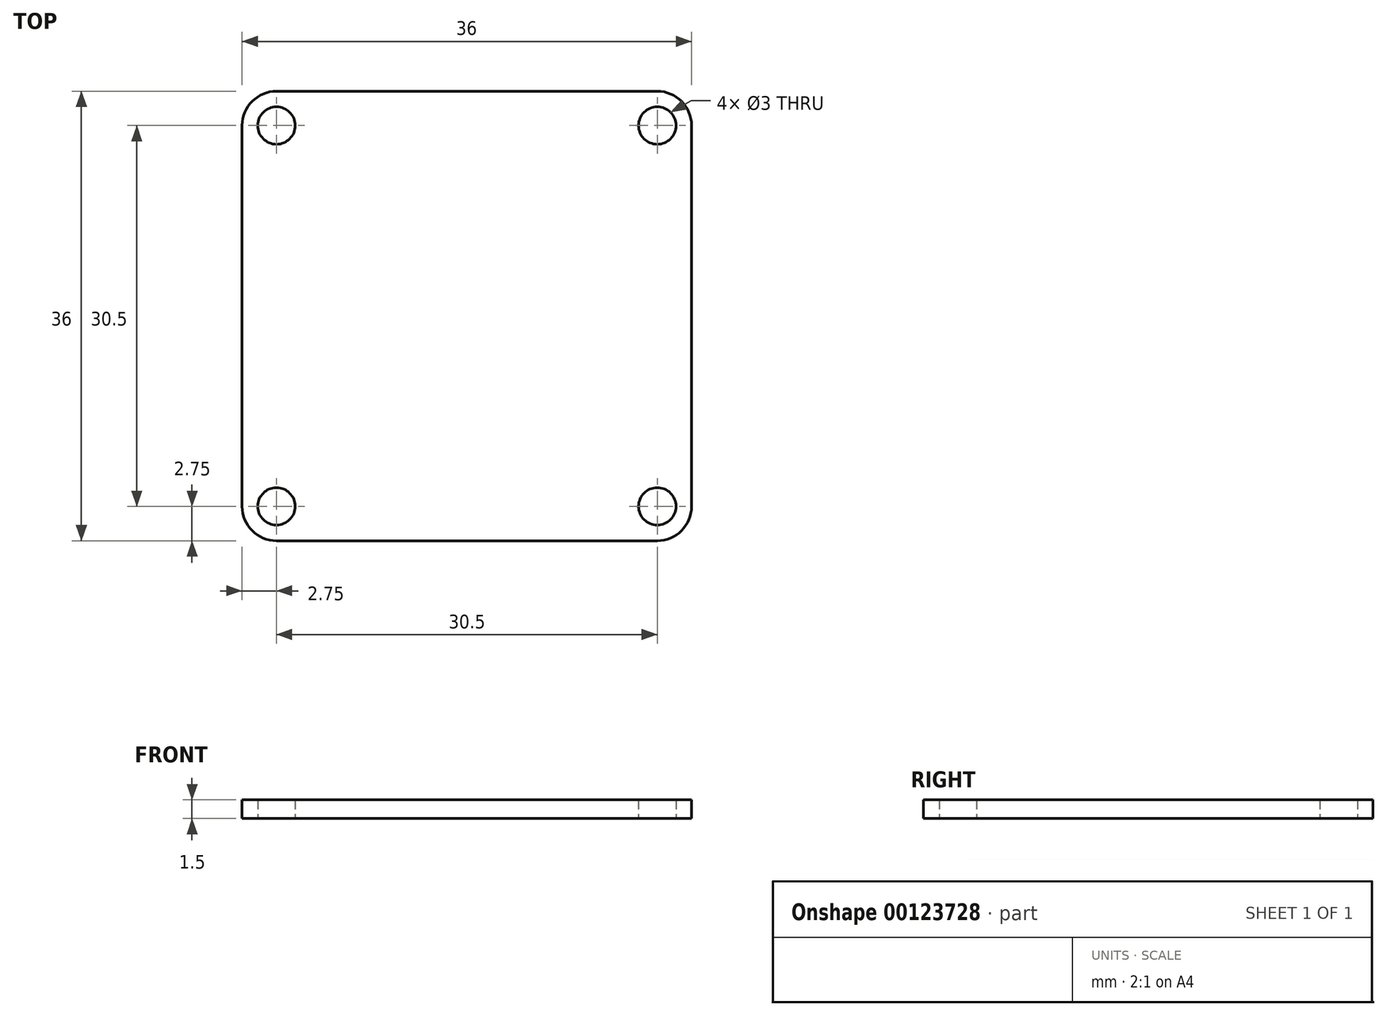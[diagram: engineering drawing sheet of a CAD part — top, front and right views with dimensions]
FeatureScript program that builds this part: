
annotation { "Feature Type Name" : "Feature", "Feature Type Description" : "" }
export const myFeature = defineFeature(function(context is Context, id is Id, definition is map)
    precondition{}
    {
        {
            var Q0;
            Q0=qCreatedBy(makeId("Top.planeOp"),FACE);
            var sketch = newSketch(context, id + "F0", { "sketchPlane" : qUnion([Q0])});
            skLineSegment(sketch, "E0.bottom", {"start": v(-15.25, 18) * mm, "end": v(15.25, 18) * mm});
            skLineSegment(sketch, "E0.top", {"start": v(-15.25, -18) * mm, "end": v(15.25, -18) * mm});
            skLineSegment(sketch, "E0.left", {"start": v(-18, 15.25) * mm, "end": v(-18, -15.25) * mm});
            skLineSegment(sketch, "E0.right", {"start": v(18, 15.25) * mm, "end": v(18, -15.25) * mm});
            skCircle(sketch, "E1", {"center": v(-15.25, 15.25) * mm, "radius": 1.5 * mm});
            skCircle(sketch, "E2.0.1.0", {"center": v(-15.25, -15.25) * mm, "radius": 1.5 * mm});
            skCircle(sketch, "E2.1.0.0", {"center": v(15.25, 15.25) * mm, "radius": 1.5 * mm});
            skCircle(sketch, "E2.1.1.0", {"center": v(15.25, -15.25) * mm, "radius": 1.5 * mm});
            skLineSegment(sketch, "E2.direction1", {"start": v(-15.25, 15.25) * mm, "end": v(15.25, 15.25) * mm, "construction": true});
            skLineSegment(sketch, "E2.direction2", {"start": v(-15.25, 15.25) * mm, "end": v(-15.25, -15.25) * mm, "construction": true});
            skPoint(sketch, "E3.visualSharp", {"position": v(-18, 18) * mm});
            skArc(sketch, "E3.filletArc", {"start": v(-15.25, 18) * mm, "mid": v(-17.2, 17.2) * mm, "end": v(-18, 15.25) * mm});
            skPoint(sketch, "E4.visualSharp", {"position": v(18, 18) * mm});
            skArc(sketch, "E4.filletArc", {"start": v(18, 15.25) * mm, "mid": v(17.2, 17.2) * mm, "end": v(15.25, 18) * mm});
            skPoint(sketch, "E5.visualSharp", {"position": v(18, -18) * mm});
            skArc(sketch, "E5.filletArc", {"start": v(15.25, -18) * mm, "mid": v(17.2, -17.2) * mm, "end": v(18, -15.25) * mm});
            skPoint(sketch, "E6.visualSharp", {"position": v(-18, -18) * mm});
            skArc(sketch, "E6.filletArc", {"start": v(-18, -15.25) * mm, "mid": v(-17.2, -17.2) * mm, "end": v(-15.25, -18) * mm});
            skSolve(sketch);
        }
        {
            var Q0;
            Q0=qSketchRegion(id+"F0",true);
            extrude(context, id + "F1", {"entities" : qUnion([Q0]), "depth" : 1.5 * mm});
        }
    });
